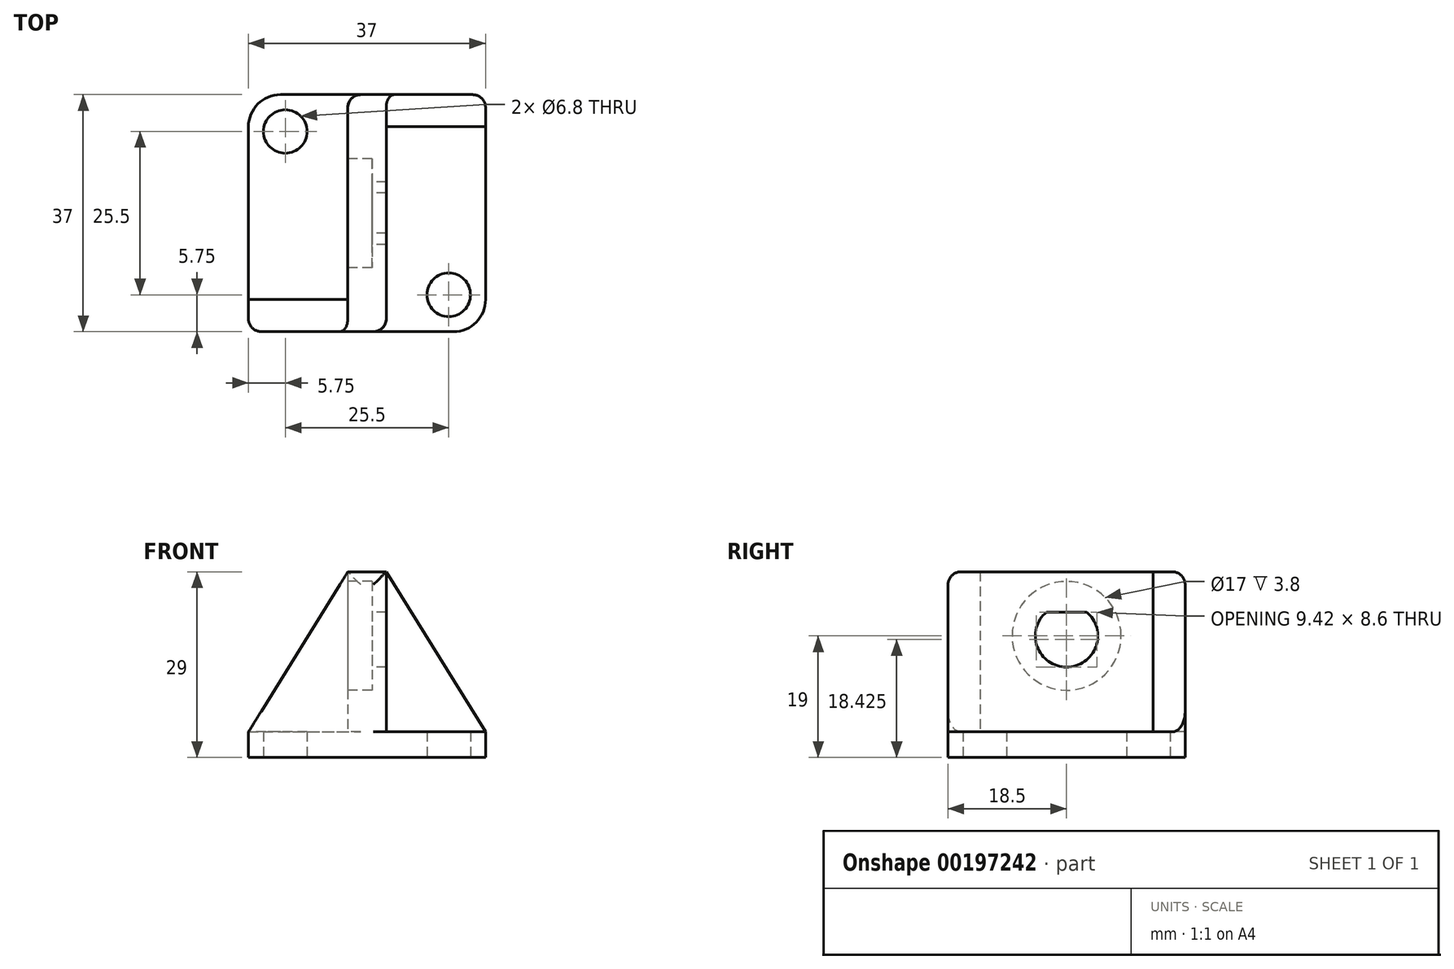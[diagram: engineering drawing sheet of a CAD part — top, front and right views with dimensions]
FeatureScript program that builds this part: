
annotation { "Feature Type Name" : "Feature", "Feature Type Description" : "" }
export const myFeature = defineFeature(function(context is Context, id is Id, definition is map)
    precondition{}
    {
        {
            var Q0;
            Q0=qCreatedBy(makeId("Top.planeOp"),FACE);
            var sketch = newSketch(context, id + "F0", { "sketchPlane" : qUnion([Q0])});
            skLineSegment(sketch, "E0.bottom", {"start": v(-12.75, 12.75) * mm, "end": v(12.75, 12.75) * mm, "construction": true});
            skLineSegment(sketch, "E0.top", {"start": v(-12.75, -12.75) * mm, "end": v(12.75, -12.75) * mm, "construction": true});
            skLineSegment(sketch, "E0.left", {"start": v(-12.75, 12.75) * mm, "end": v(-12.75, -12.75) * mm, "construction": true});
            skLineSegment(sketch, "E0.right", {"start": v(12.75, 12.75) * mm, "end": v(12.75, -12.75) * mm, "construction": true});
            skCircle(sketch, "E1", {"center": v(-12.75, 12.75) * mm, "radius": 3.4 * mm});
            skCircle(sketch, "E2", {"center": v(12.75, -12.75) * mm, "radius": 3.4 * mm});
            skLineSegment(sketch, "E3.bottom", {"start": v(-18.5, 18.5) * mm, "end": v(18.5, 18.5) * mm});
            skLineSegment(sketch, "E3.top", {"start": v(-18.5, -18.5) * mm, "end": v(18.5, -18.5) * mm});
            skLineSegment(sketch, "E3.left", {"start": v(-18.5, 18.5) * mm, "end": v(-18.5, -18.5) * mm});
            skLineSegment(sketch, "E3.right", {"start": v(18.5, 18.5) * mm, "end": v(18.5, -18.5) * mm});
            skCircle(sketch, "E4", {"center": v(-12.75, 12.75) * mm, "radius": 5.75 * mm, "construction": true});
            skCircle(sketch, "E5", {"center": v(12.75, -12.75) * mm, "radius": 5.75 * mm, "construction": true});
            skSolve(sketch);
        }
        {
            var Q0;
            Q0 = qSketchRegion(id + "F0", true);
            extrude(context, id + "F1", {"entities" : qUnion([Q0]), "depth" : 4 * mm});
        }
        {
            var Q0;
            Q0=makeQuery(id+"F1.opExtrude","CAP_FACE",FACE,{"disambiguationData":[OSD([sQuery(id+"F0.wireOp",EDGE,"E1"),sQuery(id+"F0.wireOp",EDGE,"E2"),sQuery(id+"F0.wireOp",EDGE,"E3.bottom"),sQuery(id+"F0.wireOp",EDGE,"E3.top"),sQuery(id+"F0.wireOp",EDGE,"E3.left"),sQuery(id+"F0.wireOp",EDGE,"E3.right")])],"isStart":false});
            var sketch = newSketch(context, id + "F2", { "sketchPlane" : qUnion([Q0])});
            skLineSegment(sketch, "E6", {"start": v(-18.5, -18.5) * mm, "end": v(-18.5, -13.5) * mm});
            skLineSegment(sketch, "E7", {"start": v(-18.5, -13.5) * mm, "end": v(-3, -13.5) * mm});
            skLineSegment(sketch, "E8", {"start": v(-3, -13.5) * mm, "end": v(-3, 18.5) * mm});
            skLineSegment(sketch, "E9", {"start": v(-3, 18.5) * mm, "end": v(18.5, 18.5) * mm});
            skLineSegment(sketch, "E10", {"start": v(18.5, 18.5) * mm, "end": v(18.5, 13.5) * mm});
            skLineSegment(sketch, "E11", {"start": v(18.5, 13.5) * mm, "end": v(3, 13.5) * mm});
            skLineSegment(sketch, "E12", {"start": v(3, 13.5) * mm, "end": v(3, -18.5) * mm});
            skLineSegment(sketch, "E13", {"start": v(3, -18.5) * mm, "end": v(-18.5, -18.5) * mm});
            skSolve(sketch);
        }
        {
            var Q0;
            Q0 = qSketchRegion(id + "F2", true);
            extrude(context, id + "F3", {"entities" : qUnion([Q0]), "operationType" : NewBodyOperationType.ADD, "depth" : 25 * mm});
        }
        {
            var Q0;
            Q0=makeQuery(id+"F3.boolean.opBoolean","MERGE",FACE,{"derivedFrom":[makeQuery(id+"F1.opExtrude","SWEPT_FACE",FACE,{"disambiguationData":[OSD([sQuery(id+"F0.wireOp",EDGE,"E3.top")])]}),makeQuery(id+"F3.opExtrude","SWEPT_FACE",FACE,{"disambiguationData":[OSD([sQuery(id+"F2.wireOp",EDGE,"E13")])]})]});
            var sketch = newSketch(context, id + "F4", { "sketchPlane" : qUnion([Q0])});
            skLineSegment(sketch, "E14", {"start": v(-18.5, 29) * mm, "end": v(-3, 29) * mm});
            skLineSegment(sketch, "E15", {"start": v(-3, 29) * mm, "end": v(-18.5, 4) * mm});
            skLineSegment(sketch, "E16", {"start": v(-18.5, 4) * mm, "end": v(-18.5, 29) * mm});
            skLineSegment(sketch, "E17", {"start": v(3, 29) * mm, "end": v(18.5, 29) * mm});
            skLineSegment(sketch, "E18", {"start": v(18.5, 29) * mm, "end": v(18.5, 4) * mm});
            skLineSegment(sketch, "E19", {"start": v(18.5, 4) * mm, "end": v(3, 29) * mm});
            skSolve(sketch);
        }
        {
            var Q0;
            Q0 = qSketchRegion(id + "F4", true);
            extrude(context, id + "F5", {"entities" : qUnion([Q0]), "operationType" : NewBodyOperationType.REMOVE, "endBound" : BoundingType.THROUGH_ALL, "oppositeDirection" : true, "depth" : 25 * mm});
        }
        {
            var Q0;
            Q0=makeQuery(id+"F3.opExtrude","SWEPT_FACE",FACE,{"disambiguationData":[OSD([sQuery(id+"F2.wireOp",EDGE,"E8")])]});
            var sketch = newSketch(context, id + "F6", { "sketchPlane" : qUnion([Q0])});
            skArc(sketch, "E20", {"start": v(-3.14, 22.72) * mm, "mid": v(0, 14.12) * mm, "end": v(3.14, 22.72) * mm});
            skLineSegment(sketch, "E21", {"start": v(-3.14, 22.72) * mm, "end": v(3.14, 22.72) * mm});
            skLineSegment(sketch, "E22", {"start": v(-6.19, 14.12) * mm, "end": v(8.23, 14.12) * mm, "construction": true});
            skSolve(sketch);
        }
        {
            var Q0;
            Q0 = qSketchRegion(id + "F6", true);
            extrude(context, id + "F7", {"entities" : qUnion([Q0]), "operationType" : NewBodyOperationType.REMOVE, "endBound" : BoundingType.THROUGH_ALL, "oppositeDirection" : true, "depth" : 25 * mm});
        }
        {
            var Q0;
            Q0=makeQuery(id+"F3.opExtrude","SWEPT_FACE",FACE,{"disambiguationData":[OSD([sQuery(id+"F2.wireOp",EDGE,"E8")])]});
            var sketch = newSketch(context, id + "F8", { "sketchPlane" : qUnion([Q0])});
            skCircle(sketch, "E23", {"center": v(0, 19) * mm, "radius": 8.5 * mm});
            skSolve(sketch);
        }
        {
            var Q0;
            Q0 = qSketchRegion(id + "F8", true);
            extrude(context, id + "F9", {"entities" : qUnion([Q0]), "operationType" : NewBodyOperationType.REMOVE, "oppositeDirection" : true, "depth" : 3.8 * mm});
        }
        {
            var Q0;
            Q0=makeQuery(id+"F1.opExtrude","SWEPT_EDGE",EDGE,{"disambiguationData":[OSD([sQuery(id+"F0.wireOp",EDGE,"E3.bottom"),sQuery(id+"F0.wireOp",EDGE,"E3.left")])]});
            var Q1;
            Q1=makeQuery(id+"F1.opExtrude","SWEPT_EDGE",EDGE,{"disambiguationData":[OSD([sQuery(id+"F0.wireOp",EDGE,"E3.top"),sQuery(id+"F0.wireOp",EDGE,"E3.right")])]});
            fillet(context, id + "F10", {"entities" : qUnion([Q0, Q1]), "radius" : 5 * mm, "tangentPropagation" : true, "allowEdgeOverflow" : false});
        }
        {
            var Q0;
            Q0=makeQuery(id+"F3.opExtrude","CAP_EDGE",EDGE,{"disambiguationData":[OSD([sQuery(id+"F2.wireOp",EDGE,"E13")])],"isStart":false});
            var Q1;
            Q1=makeQuery(id+"F3.opExtrude","CAP_EDGE",EDGE,{"disambiguationData":[OSD([sQuery(id+"F2.wireOp",EDGE,"E9")])],"isStart":false});
            var Q2;
            Q2=makeQuery(id+"F3.boolean.opBoolean","MERGE",EDGE,{"derivedFrom":[makeQuery(id+"F1.opExtrude","SWEPT_EDGE",EDGE,{"disambiguationData":[OSD([sQuery(id+"F0.wireOp",EDGE,"E3.top"),sQuery(id+"F0.wireOp",EDGE,"E3.left")])]}),makeQuery(id+"F3.opExtrude","SWEPT_EDGE",EDGE,{"disambiguationData":[OSD([sQuery(id+"F2.wireOp",EDGE,"E6"),sQuery(id+"F2.wireOp",EDGE,"E13")])]})]});
            var Q3;
            Q3=makeQuery(id+"F3.boolean.opBoolean","MERGE",EDGE,{"derivedFrom":[makeQuery(id+"F1.opExtrude","SWEPT_EDGE",EDGE,{"disambiguationData":[OSD([sQuery(id+"F0.wireOp",EDGE,"E3.bottom"),sQuery(id+"F0.wireOp",EDGE,"E3.right")])]}),makeQuery(id+"F3.opExtrude","SWEPT_EDGE",EDGE,{"disambiguationData":[OSD([sQuery(id+"F2.wireOp",EDGE,"E9"),sQuery(id+"F2.wireOp",EDGE,"E10")])]})]});
            var Q4;
            Q4=makeQuery(id+"F3.opExtrude","SWEPT_EDGE",EDGE,{"disambiguationData":[OSD([sQuery(id+"F0.wireOp",EDGE,"E3.bottom"),sQuery(id+"F2.wireOp",EDGE,"E8"),sQuery(id+"F2.wireOp",EDGE,"E9")])]});
            var Q5;
            Q5=makeQuery(id+"F3.opExtrude","SWEPT_EDGE",EDGE,{"disambiguationData":[OSD([sQuery(id+"F0.wireOp",EDGE,"E3.top"),sQuery(id+"F2.wireOp",EDGE,"E12"),sQuery(id+"F2.wireOp",EDGE,"E13")])]});
            fillet(context, id + "F11", {"entities" : qUnion([Q0, Q1, Q2, Q3, Q4, Q5]), "radius" : 2 * mm, "tangentPropagation" : true, "allowEdgeOverflow" : false});
        }
    });
